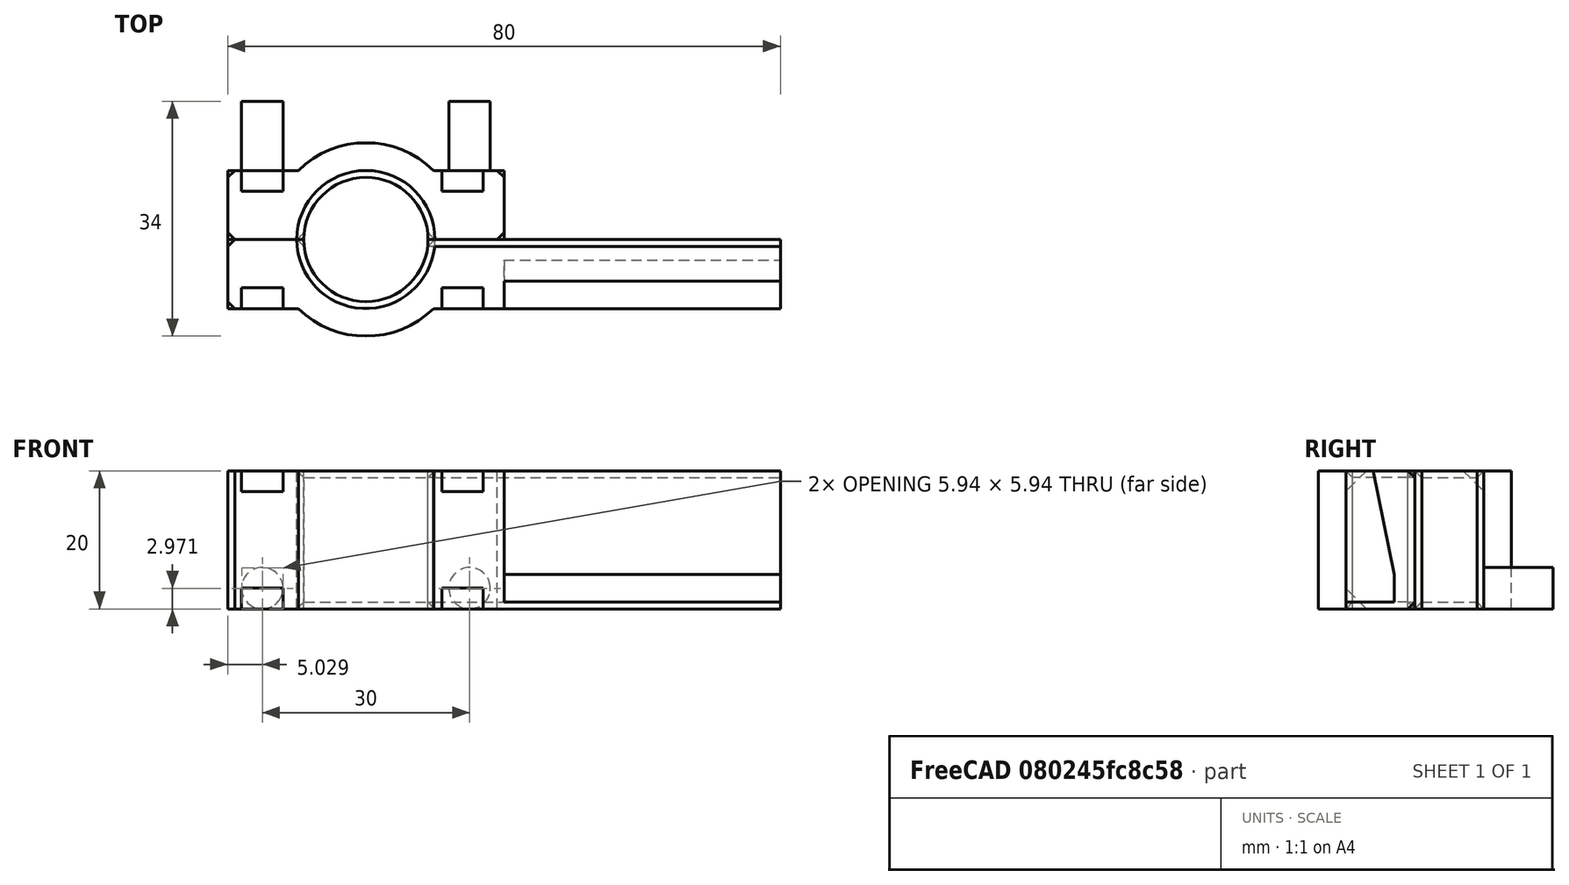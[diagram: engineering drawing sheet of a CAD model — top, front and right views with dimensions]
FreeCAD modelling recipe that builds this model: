
FCSTD DOCUMENT  (FreeCAD 0.18R16146 (Git))
Label: webcam-mounter
License: All rights reserved
LicenseURL: http://en.wikipedia.org/wiki/All_rights_reserved
objects: Part::Cut×9, Part::Box×8, Part::Cylinder×6, Part::Chamfer×6, Part::Feature×5, Part::MultiFuse×4
note: 38 computed .brp shape members not serialized (recipe doc carries the construction recipe); baked Part::Feature solids carry a one-line shape summary decoded from their .brp

FEATURE [Part::Cylinder] Cylinder
  Angle = 360
  AttacherType = Attacher::AttachEngine3D
  Height = 20
  Radius = 9
FEATURE [Part::Box] Box  label="Cube"
  AttacherType = Attacher::AttachEngine3D
  Height = 20
  Length = 80
  Placement = pos=(-20,-10,0) rot=(0,0,1;0rad)
  Width = 10
FEATURE [Part::Box] Box001  label="Cube001"
  AttacherType = Attacher::AttachEngine3D
  Height = 20
  Length = 40
  Placement = pos=(-20,0,0) rot=(0,0,1;0rad)
  Width = 10
FEATURE [Part::Cylinder] Cylinder001
  Angle = 360
  AttacherType = Attacher::AttachEngine3D
  Height = 20
  Radius = 14
FEATURE [Part::Cylinder] Cylinder002
  Angle = 360
  AttacherType = Attacher::AttachEngine3D
  Height = 20
  Radius = 14
FEATURE [Part::Cylinder] Cylinder003
  Angle = 360
  AttacherType = Attacher::AttachEngine3D
  Height = 20
  Radius = 9
FEATURE [Part::Box] Box002  label="Cube002"
  AttacherType = Attacher::AttachEngine3D
  Height = 20
  Length = 40
  Placement = pos=(-20,-15,0) rot=(0,0,1;0rad)
  Width = 15
FEATURE [Part::Box] Box003  label="Cube003"
  AttacherType = Attacher::AttachEngine3D
  Height = 20
  Length = 40
  Placement = pos=(-20,0,0) rot=(0,0,1;0rad)
  Width = 15
FEATURE [Part::Cut] Cut
  Base = -> Cylinder002
  Tool = -> Box003
FEATURE [Part::Cut] Cut001
  Base = -> Cylinder001
  Tool = -> Box002
FEATURE [Part::MultiFuse] Fusion
  Shapes = -> [Box,Cut]
FEATURE [Part::Cut] Cut002
  Base = -> Fusion
  Tool = -> Cylinder
FEATURE [Part::MultiFuse] Fusion001
  Shapes = -> [Box001,Cut001]
FEATURE [Part::Cut] Cut003
  Base = -> Fusion001
  Tool = -> Cylinder003
FEATURE [Part::Box] Box004  label="Cube004"
  AttacherType = Attacher::AttachEngine3D
  Height = 19
  Length = 40
  Placement = pos=(20,-13,1) rot=(0,0,1;0rad)
  Width = 10
FEATURE [Part::Chamfer] Chamfer
  Base = -> Box004
  Edges = 1 edges: [Edge12 r1=15 r2=3]
FEATURE [Part::Cut] Cut004
  Base = -> Cut002
  Tool = -> Chamfer
FEATURE [Part::Cylinder] Cylinder004
  Angle = 360
  AttacherType = Attacher::AttachEngine3D
  Height = 10
  Placement = pos=(-15,20,3) rot=(1,0,0;1.5708rad)
  Radius = 3
FEATURE [Part::Cylinder] Cylinder005
  Angle = 360
  AttacherType = Attacher::AttachEngine3D
  Height = 10
  Placement = pos=(15,20,3) rot=(1,0,0;1.5708rad)
  Radius = 3
FEATURE [Part::Box] Box005  label="Cube005"
  AttacherType = Attacher::AttachEngine3D
  Height = 6
  Length = 6
  Placement = pos=(-18,-16,0) rot=(0,0,1;0rad)
  Width = 6
FEATURE [Part::Box] Box007  label="Cube007"
  AttacherType = Attacher::AttachEngine3D
  Height = 6
  Length = 6
  Placement = pos=(-18,-16,20) rot=(0,0,1;0rad)
  Width = 6
FEATURE [Part::Box] Box008  label="Cube008"
  AttacherType = Attacher::AttachEngine3D
  Height = 6
  Length = 6
  Placement = pos=(-18,10,20) rot=(0,0,1;0rad)
  Width = 6
FEATURE [Part::Chamfer] Chamfer001
  Base = -> Box008
  Edges = 1 edges r=3: [Edge9]
  Placement = pos=(0,-3,-3) rot=(0,0,1;0rad)
FEATURE [Part::Chamfer] Chamfer002
  Base = -> Box007
  Edges = 1 edges r=3: [Edge11]
  Placement = pos=(0,3,-3) rot=(0,0,1;0rad)
FEATURE [Part::Chamfer] Chamfer003
  Base = -> Box005
  Edges = 1 edges r=3: [Edge12]
  Placement = pos=(0,3,-3) rot=(0,0,1;0rad)
FEATURE [Part::MultiFuse] Fusion002
  Shapes = -> [Chamfer001,Chamfer002,Chamfer003]
FEATURE [Part::Feature] Fusion002001  label="Fusion003"
  Placement = pos=(29,0,0) rot=(0,0,1;0rad)
  shape: bbox 6 x 26 x 26 mm, 21 faces, 3 solids (baked)
FEATURE [Part::Feature] Fusion002002  label="Fusion004"
  shape: bbox 6 x 26 x 26 mm, 21 faces, 3 solids (baked)
FEATURE [Part::Feature] Fusion002001001  label="Fusion005"
  Placement = pos=(29,0,0) rot=(0,0,1;0rad)
  shape: bbox 6 x 26 x 26 mm, 21 faces, 3 solids (baked)
FEATURE [Part::Cut] Cut005
  Base = -> Cut003
  Tool = -> Fusion002002
FEATURE [Part::Cut] Cut006
  Base = -> Cut005
  Tool = -> Fusion002001001
FEATURE [Part::Cut] Cut007
  Base = -> Cut004
  Tool = -> Fusion002
FEATURE [Part::Cut] Cut008
  Base = -> Cut007
  Tool = -> Fusion002001
FEATURE [Part::MultiFuse] Fusion002001002
  Shapes = -> [Cut006,Cylinder004,Cylinder005]
FEATURE [Part::Feature] Cut008001  label="Cut009"
  shape: bbox 80 x 14 x 20 mm, 26 faces (baked)
FEATURE [Part::Chamfer] Chamfer004
  Base = -> Cut008001
  Edges = 8 edges r=1: [Edge1,Edge3,Edge65,Edge66,Edge68,Edge69,Edge70,Edge72]
FEATURE [Part::Feature] Fusion002001002001  label="Fusion002001003"
  shape: bbox 40 x 20 x 20 mm, 20 faces (baked)
FEATURE [Part::Chamfer] Chamfer005
  Base = -> Fusion002001002001
  Edges = 8 edges r=1: [Edge13,Edge22,Edge27,Edge35,Edge46,Edge48,Edge49,Edge50]
